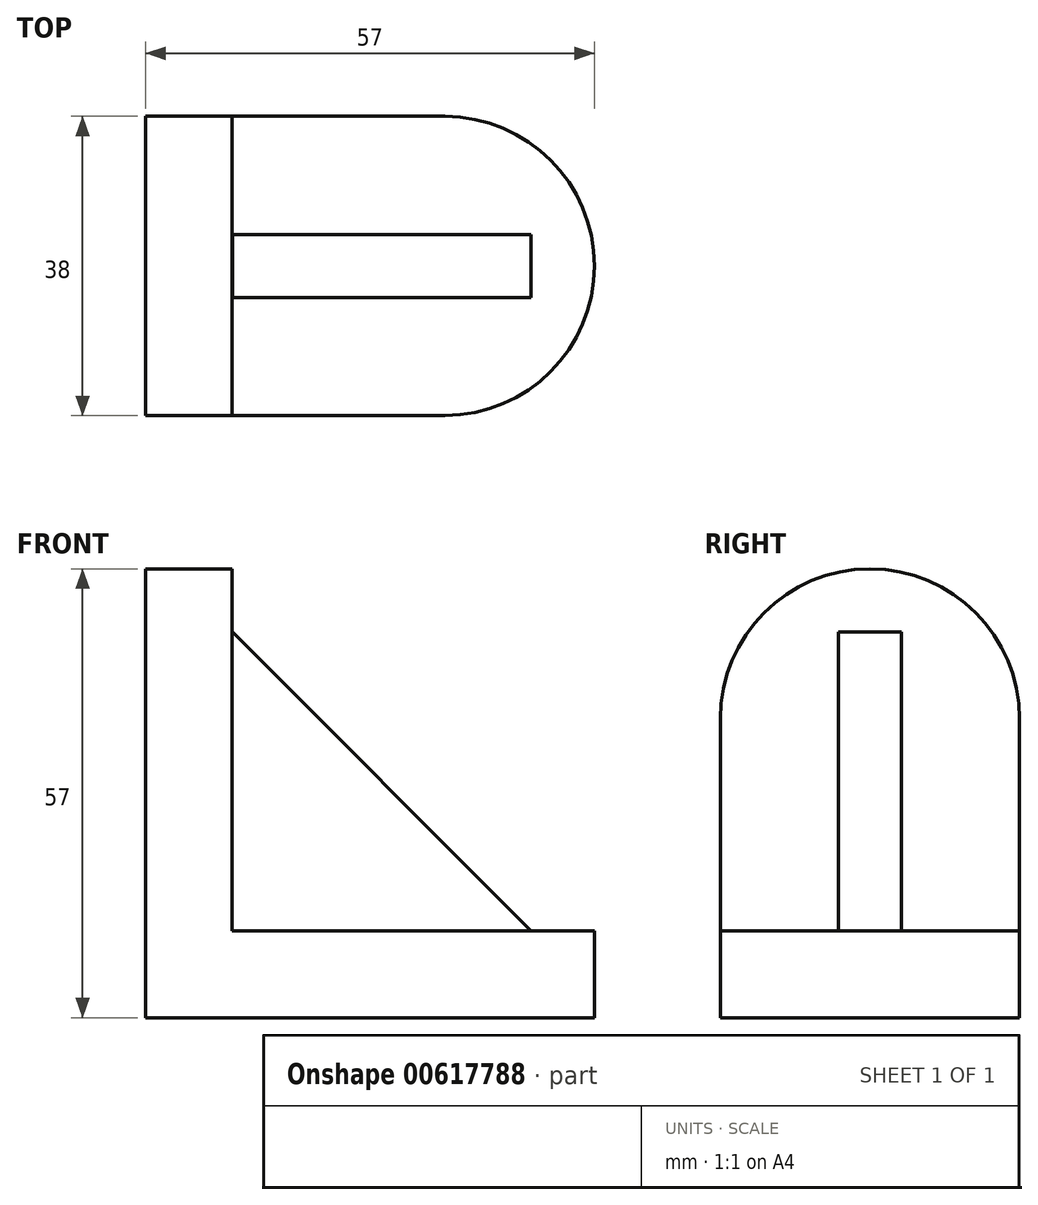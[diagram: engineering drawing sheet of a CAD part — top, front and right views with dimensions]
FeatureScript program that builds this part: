
annotation { "Feature Type Name" : "Feature", "Feature Type Description" : "" }
export const myFeature = defineFeature(function(context is Context, id is Id, definition is map)
    precondition{}
    {
        {
            var Q0;
            Q0=qCreatedBy(makeId("Top.planeOp"),FACE);
            var sketch = newSketch(context, id + "F0", { "sketchPlane" : qUnion([Q0])});
            skLineSegment(sketch, "E0", {"start": v(0, 0) * mm, "end": v(38, 0) * mm});
            skLineSegment(sketch, "E1", {"start": v(38, 38) * mm, "end": v(0, 38) * mm});
            skLineSegment(sketch, "E2", {"start": v(0, 38) * mm, "end": v(0, 0) * mm});
            skArc(sketch, "E3", {"start": v(38, 0) * mm, "mid": v(57, 19) * mm, "end": v(38, 38) * mm});
            skSolve(sketch);
        }
        {
            var Q0;
            Q0=qCreatedBy(makeId("Right.planeOp"),FACE);
            var sketch = newSketch(context, id + "F1", { "sketchPlane" : qUnion([Q0])});
            skLineSegment(sketch, "E4.bottom", {"start": v(0, 0) * mm, "end": v(38, 0) * mm});
            skLineSegment(sketch, "E4.top", {"start": v(0, 38) * mm, "end": v(38, 38) * mm});
            skLineSegment(sketch, "E4.left", {"start": v(0, 0) * mm, "end": v(0, 38) * mm});
            skLineSegment(sketch, "E4.right", {"start": v(38, 0) * mm, "end": v(38, 38) * mm});
            skArc(sketch, "E5", {"start": v(38, 38) * mm, "mid": v(19, 57) * mm, "end": v(0, 38) * mm});
            skSolve(sketch);
        }
        {
            var Q0;
            Q0=makeQuery(id+"F1.imprint","IMPRINT",FACE,{"disambiguationData":[TD([[makeQuery(id+"F1.imprint","IMPRINT",EDGE,{"derivedFrom":sQuery(id+"F1.wireOp",EDGE,"E4.bottom")}),1.0]])]});
            var Q1;
            Q1=makeQuery(id+"F1.imprint","IMPRINT",FACE,{"disambiguationData":[TD([[makeQuery(id+"F1.imprint","IMPRINT",EDGE,{"derivedFrom":sQuery(id+"F1.wireOp",EDGE,"E4.top")}),1.0]])]});
            extrude(context, id + "F2", {"entities" : qUnion([Q0, Q1]), "depth" : 11 * mm, "offsetDistance" : 25.4 * mm});
        }
        {
            var Q0;
            Q0=makeQuery(id+"F0.imprint","IMPRINT",FACE,{"disambiguationData":[TD([[makeQuery(id+"F0.imprint","IMPRINT",EDGE,{"derivedFrom":sQuery(id+"F0.wireOp",EDGE,"E0")}),1.0]])]});
            extrude(context, id + "F3", {"entities" : qUnion([Q0]), "operationType" : NewBodyOperationType.ADD, "depth" : 11 * mm, "offsetDistance" : 25.4 * mm});
        }
        {
            var Q0;
            Q0=makeQuery(id+"F3.opExtrude","CAP_EDGE",EDGE,{"disambiguationData":[OSD([sQuery(id+"F0.wireOp",EDGE,"E3")])],"isStart":false});
            cPoint(context, id + "F4", {"entities" : qUnion([Q0]), "parameter" : 0.5});
        }
        {
            var Q0;
            Q0=makeQuery(id+"F3.boolean.opBoolean","INTERSECT",EDGE,{"derivedFrom":[makeQuery(id+"F2.opExtrude","CAP_FACE",FACE,{"disambiguationData":[OSD([sQuery(id+"F1.wireOp",EDGE,"E4.bottom"),sQuery(id+"F1.wireOp",EDGE,"E4.left"),sQuery(id+"F1.wireOp",EDGE,"E4.right"),sQuery(id+"F1.wireOp",EDGE,"E5")])],"isStart":false}),makeQuery(id+"F3.opExtrude","CAP_FACE",FACE,{"disambiguationData":[OSD([sQuery(id+"F0.wireOp",EDGE,"E0"),sQuery(id+"F0.wireOp",EDGE,"E1"),sQuery(id+"F0.wireOp",EDGE,"E2"),sQuery(id+"F0.wireOp",EDGE,"E3")])],"isStart":false})]});
            cPoint(context, id + "F5", {"entities" : qUnion([Q0]), "parameter" : 0.5});
        }
        {
            var Q0;
            Q0=makeQuery(id+"F2.opExtrude","CAP_EDGE",EDGE,{"disambiguationData":[OSD([sQuery(id+"F1.wireOp",EDGE,"E5")])],"isStart":false});
            cPoint(context, id + "F6", {"entities" : qUnion([Q0]), "parameter" : 0.5});
        }
        {
            var Q0;
            Q0=qCreatedBy(id+"F4",VERTEX);
            var Q1;
            Q1=qCreatedBy(id+"F5",VERTEX);
            var Q2;
            Q2=qCreatedBy(id+"F6",VERTEX);
            cPlane(context, id + "F7", {"entities" : qUnion([Q0, Q1, Q2]), "cplaneType" : CPlaneType.THREE_POINT, "offset" : 25.4 * mm, "width" : 152.4 * mm, "height" : 152.4 * mm});
        }
        {
            var Q0;
            Q0=qCreatedBy(id+"F7.planeOp",FACE);
            var sketch = newSketch(context, id + "F8", { "sketchPlane" : qUnion([Q0])});
            skPoint(sketch, "E6", {"position": v(49, 10.98) * mm});
            skPoint(sketch, "E7", {"position": v(11.04, 49) * mm});
            skLineSegment(sketch, "E8", {"start": v(11.04, 49) * mm, "end": v(49, 10.98) * mm});
            skSolve(sketch);
        }
        {
            var Q0;
            Q0=sQuery(id+"F8.wireOp",EDGE,"E8");
            extrude(context, id + "F9", {"bodyType" : ToolBodyType.SURFACE, "surfaceEntities" : qUnion([Q0]), "endBound" : BoundingType.SYMMETRIC, "depth" : 8 * mm, "offsetDistance" : 25.4 * mm});
        }
        {
            var Q0;
            Q0=makeQuery(id+"F9.opExtrude","SWEPT_FACE",FACE,{"disambiguationData":[OSD([sQuery(id+"F8.wireOp",EDGE,"E8")])]});
            var Q1;
            Q1=makeQuery(id+"F2.opExtrude","SWEPT_BODY",BODY,{"disambiguationData":[OSD([sQuery(id+"F1.wireOp",EDGE,"E4.bottom"),sQuery(id+"F1.wireOp",EDGE,"E4.left"),sQuery(id+"F1.wireOp",EDGE,"E4.right"),sQuery(id+"F1.wireOp",EDGE,"E5")])]});
            extrude(context, id + "F10", {"entities" : qUnion([Q0]), "operationType" : NewBodyOperationType.ADD, "endBound" : BoundingType.UP_TO_BODY, "depth" : 25.4 * mm, "endBoundEntityBody" : qUnion([Q1]), "offsetDistance" : 25.4 * mm});
        }
    });
